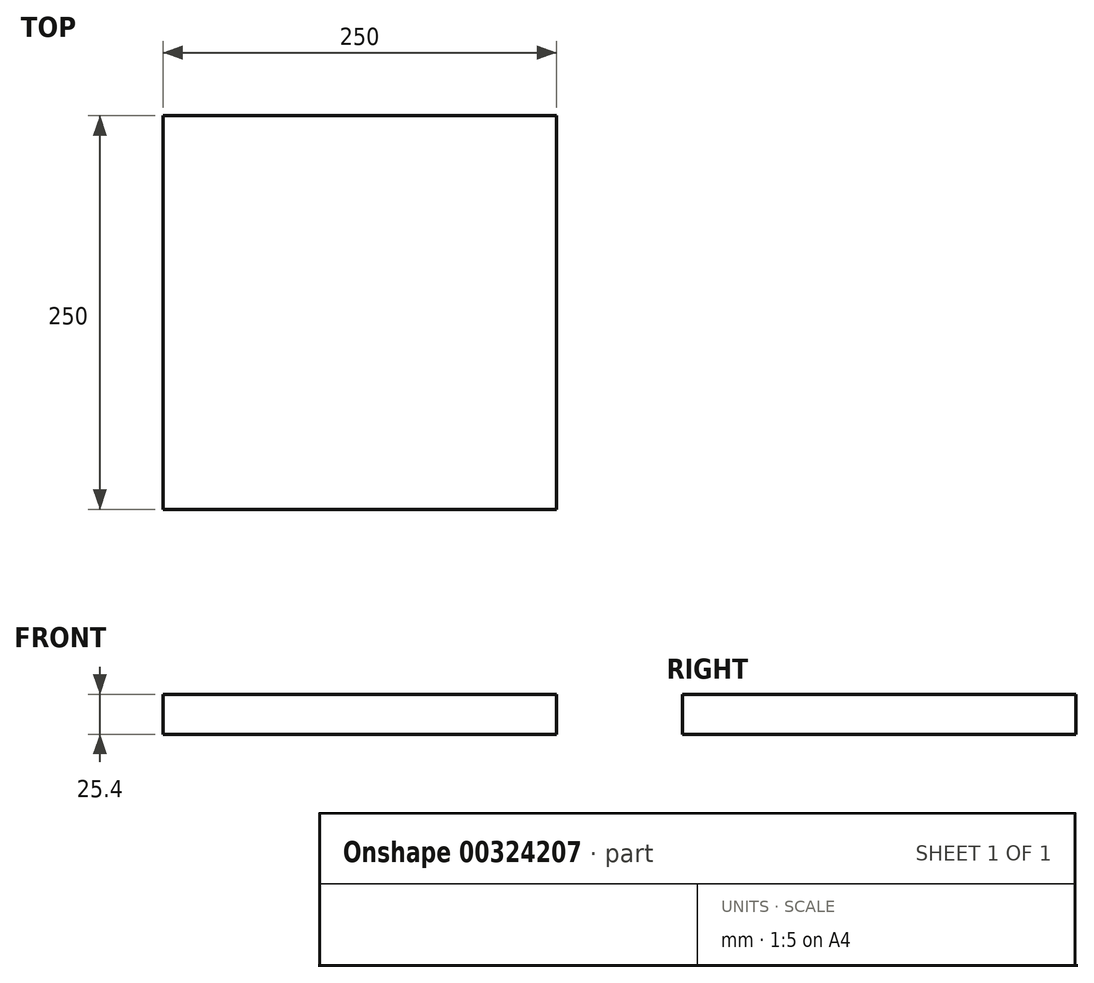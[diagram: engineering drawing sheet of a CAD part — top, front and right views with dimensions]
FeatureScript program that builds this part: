
annotation { "Feature Type Name" : "Feature", "Feature Type Description" : "" }
export const myFeature = defineFeature(function(context is Context, id is Id, definition is map)
    precondition{}
    {
        {
            var Q0;
            Q0=qCreatedBy(makeId("Top.planeOp"),FACE);
            var sketch = newSketch(context, id + "F0", { "sketchPlane" : qUnion([Q0])});
            skLineSegment(sketch, "E0.bottom", {"start": v(-75.51, 173.32) * mm, "end": v(174.49, 173.32) * mm});
            skLineSegment(sketch, "E0.top", {"start": v(-75.51, -76.68) * mm, "end": v(174.49, -76.68) * mm});
            skLineSegment(sketch, "E0.left", {"start": v(-75.51, 173.32) * mm, "end": v(-75.51, -76.68) * mm});
            skLineSegment(sketch, "E0.right", {"start": v(174.49, 173.32) * mm, "end": v(174.49, -76.68) * mm});
            skSolve(sketch);
        }
        {
            var Q0;
            Q0=makeQuery(id+"F0.imprint","IMPRINT",FACE,{"disambiguationData":[TD([[makeQuery(id+"F0.imprint","IMPRINT",EDGE,{"derivedFrom":sQuery(id+"F0.wireOp",EDGE,"E0.bottom")}),-1.0]])]});
            extrude(context, id + "F1", {"entities" : qUnion([Q0]), "depth" : 25.4 * mm});
        }
    });
